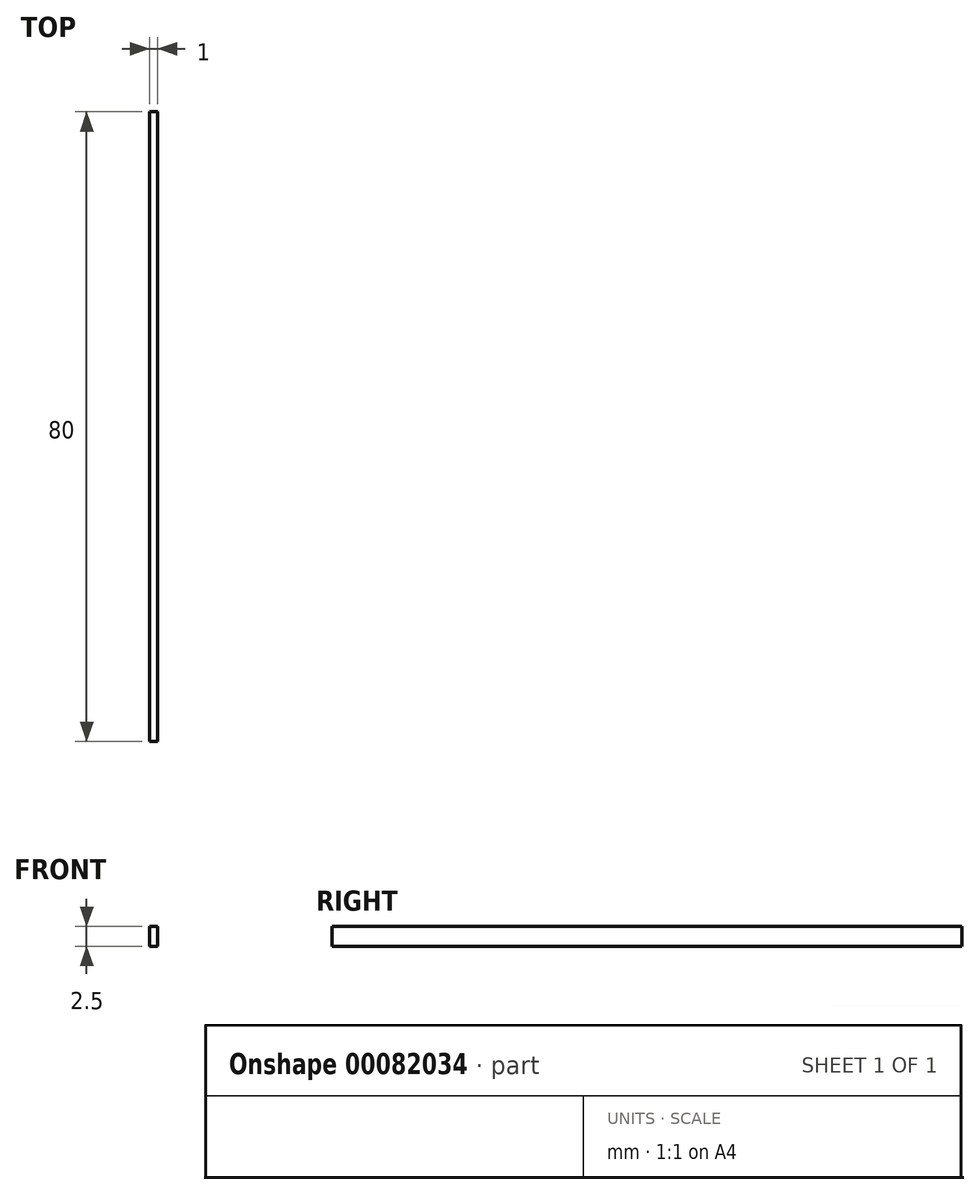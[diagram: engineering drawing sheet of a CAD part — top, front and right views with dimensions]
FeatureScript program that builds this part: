
annotation { "Feature Type Name" : "Feature", "Feature Type Description" : "" }
export const myFeature = defineFeature(function(context is Context, id is Id, definition is map)
    precondition{}
    {
        {
            var Q0;
            Q0=qCreatedBy(makeId("Front.planeOp"),FACE);
            var sketch = newSketch(context, id + "F0", { "sketchPlane" : qUnion([Q0])});
            skLineSegment(sketch, "E0.bottom", {"start": v(-0.5, -1.25) * mm, "end": v(0.5, -1.25) * mm});
            skLineSegment(sketch, "E0.top", {"start": v(-0.5, 1.25) * mm, "end": v(0.5, 1.25) * mm});
            skLineSegment(sketch, "E0.left", {"start": v(0.5, 1.25) * mm, "end": v(0.5, -1.25) * mm});
            skLineSegment(sketch, "E0.right", {"start": v(-0.5, 1.25) * mm, "end": v(-0.5, -1.25) * mm});
            skLineSegment(sketch, "E1", {"start": v(0.5, 1.25) * mm, "end": v(-0.5, -1.25) * mm, "construction": true});
            skSolve(sketch);
        }
        {
            var Q0;
            Q0 = qSketchRegion(id + "F0", true);
            extrude(context, id + "F1", {"entities" : qUnion([Q0]), "depth" : 40 * mm, "hasSecondDirection" : true, "secondDirectionOppositeDirection" : true, "secondDirectionDepth" : 40 * mm});
        }
    });
